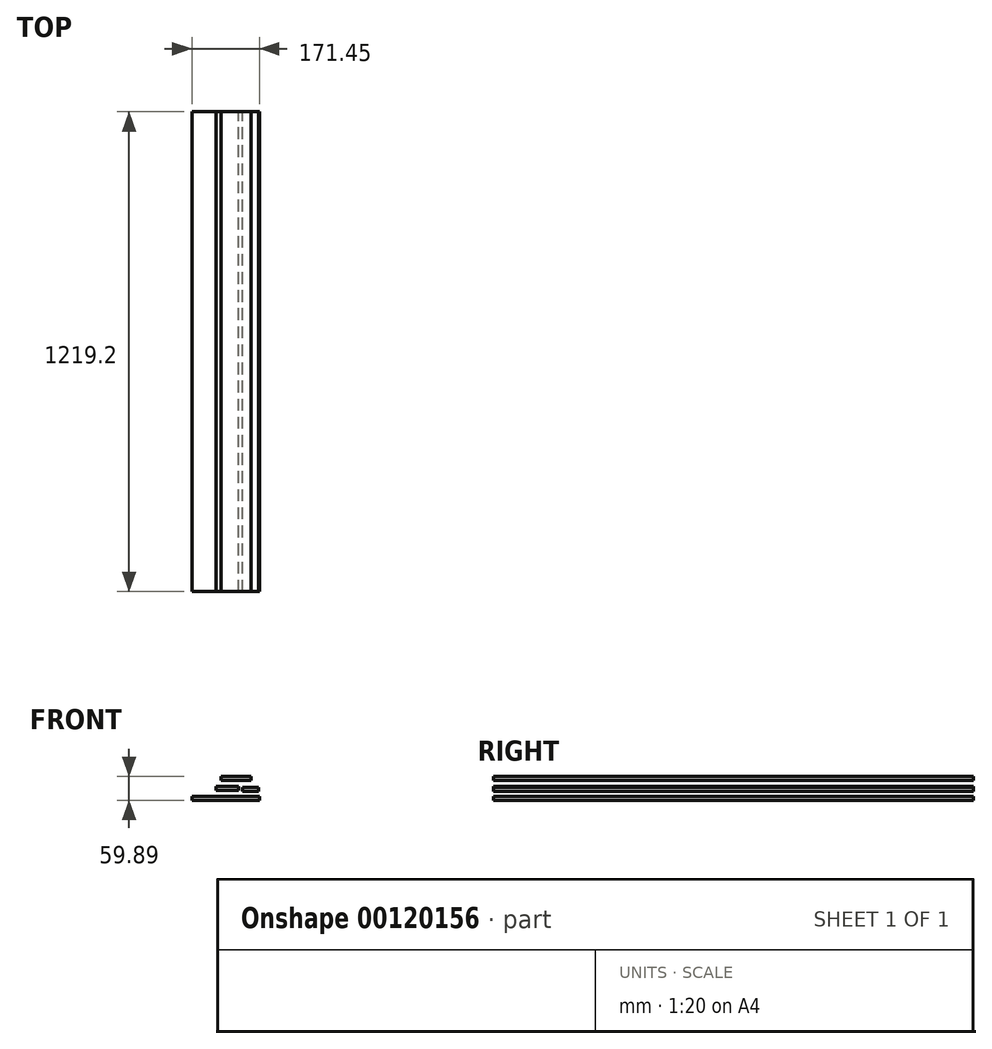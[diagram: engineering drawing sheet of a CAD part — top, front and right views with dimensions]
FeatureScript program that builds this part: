
annotation { "Feature Type Name" : "Feature", "Feature Type Description" : "" }
export const myFeature = defineFeature(function(context is Context, id is Id, definition is map)
    precondition{}
    {
        {
            var Q0;
            Q0=qCreatedBy(makeId("Front.planeOp"),FACE);
            var sketch = newSketch(context, id + "F0", { "sketchPlane" : qUnion([Q0])});
            skLineSegment(sketch, "E0.bottom", {"start": v(0, 0) * mm, "end": v(40.64, 0) * mm});
            skLineSegment(sketch, "E0.top", {"start": v(0, 9.53) * mm, "end": v(40.64, 9.53) * mm});
            skLineSegment(sketch, "E0.left", {"start": v(0, 0) * mm, "end": v(0, 9.53) * mm});
            skLineSegment(sketch, "E0.right", {"start": v(40.64, 0) * mm, "end": v(40.64, 9.53) * mm});
            skSolve(sketch);
        }
        {
            var Q0;
            Q0=makeQuery(id+"F0.imprint","IMPRINT",FACE,{"disambiguationData":[TD([[makeQuery(id+"F0.imprint","IMPRINT",EDGE,{"derivedFrom":sQuery(id+"F0.wireOp",EDGE,"E0.bottom")}),1.0]])]});
            extrude(context, id + "F1", {"entities" : qUnion([Q0]), "depth" : 1219.2 * mm});
        }
        {
            var Q0;
            Q0=qCreatedBy(makeId("Front.planeOp"),FACE);
            var sketch = newSketch(context, id + "F2", { "sketchPlane" : qUnion([Q0])});
            skLineSegment(sketch, "E1.bottom", {"start": v(-68.35, 2.1) * mm, "end": v(-11.2, 2.1) * mm});
            skLineSegment(sketch, "E1.top", {"start": v(-68.35, 11.63) * mm, "end": v(-11.2, 11.63) * mm});
            skLineSegment(sketch, "E1.left", {"start": v(-68.35, 2.1) * mm, "end": v(-68.35, 11.63) * mm});
            skLineSegment(sketch, "E1.right", {"start": v(-11.2, 2.1) * mm, "end": v(-11.2, 11.63) * mm});
            skSolve(sketch);
        }
        {
            var Q0;
            Q0=makeQuery(id+"F2.imprint","IMPRINT",FACE,{"disambiguationData":[TD([[makeQuery(id+"F2.imprint","IMPRINT",EDGE,{"derivedFrom":sQuery(id+"F2.wireOp",EDGE,"E1.bottom")}),1.0]])]});
            extrude(context, id + "F3", {"entities" : qUnion([Q0]), "depth" : 1219.2 * mm});
        }
        {
            var Q0;
            Q0=qCreatedBy(makeId("Front.planeOp"),FACE);
            var sketch = newSketch(context, id + "F4", { "sketchPlane" : qUnion([Q0])});
            skLineSegment(sketch, "E2.bottom", {"start": v(-129.15, -13.42) * mm, "end": v(42.3, -13.42) * mm});
            skLineSegment(sketch, "E2.top", {"start": v(-129.15, -22.95) * mm, "end": v(42.3, -22.95) * mm});
            skLineSegment(sketch, "E2.left", {"start": v(-129.15, -13.42) * mm, "end": v(-129.15, -22.95) * mm});
            skLineSegment(sketch, "E2.right", {"start": v(42.3, -13.42) * mm, "end": v(42.3, -22.95) * mm});
            skSolve(sketch);
        }
        {
            var Q0;
            Q0=makeQuery(id+"F4.imprint","IMPRINT",FACE,{"disambiguationData":[TD([[makeQuery(id+"F4.imprint","IMPRINT",EDGE,{"derivedFrom":sQuery(id+"F4.wireOp",EDGE,"E2.bottom")}),-1.0]])]});
            extrude(context, id + "F5", {"entities" : qUnion([Q0]), "depth" : 1219.2 * mm});
        }
        {
            var Q0;
            Q0=qCreatedBy(makeId("Front.planeOp"),FACE);
            var sketch = newSketch(context, id + "F6", { "sketchPlane" : qUnion([Q0])});
            skLineSegment(sketch, "E3.bottom", {"start": v(-55.87, 27.41) * mm, "end": v(20.33, 27.41) * mm});
            skLineSegment(sketch, "E3.top", {"start": v(-55.87, 36.94) * mm, "end": v(20.33, 36.94) * mm});
            skLineSegment(sketch, "E3.left", {"start": v(-55.87, 27.41) * mm, "end": v(-55.87, 36.94) * mm});
            skLineSegment(sketch, "E3.right", {"start": v(20.33, 27.41) * mm, "end": v(20.33, 36.94) * mm});
            skSolve(sketch);
        }
        {
            var Q0;
            Q0=makeQuery(id+"F6.imprint","IMPRINT",FACE,{"disambiguationData":[TD([[makeQuery(id+"F6.imprint","IMPRINT",EDGE,{"derivedFrom":sQuery(id+"F6.wireOp",EDGE,"E3.bottom")}),1.0]])]});
            extrude(context, id + "F7", {"entities" : qUnion([Q0]), "depth" : 1219.2 * mm});
        }
    });
